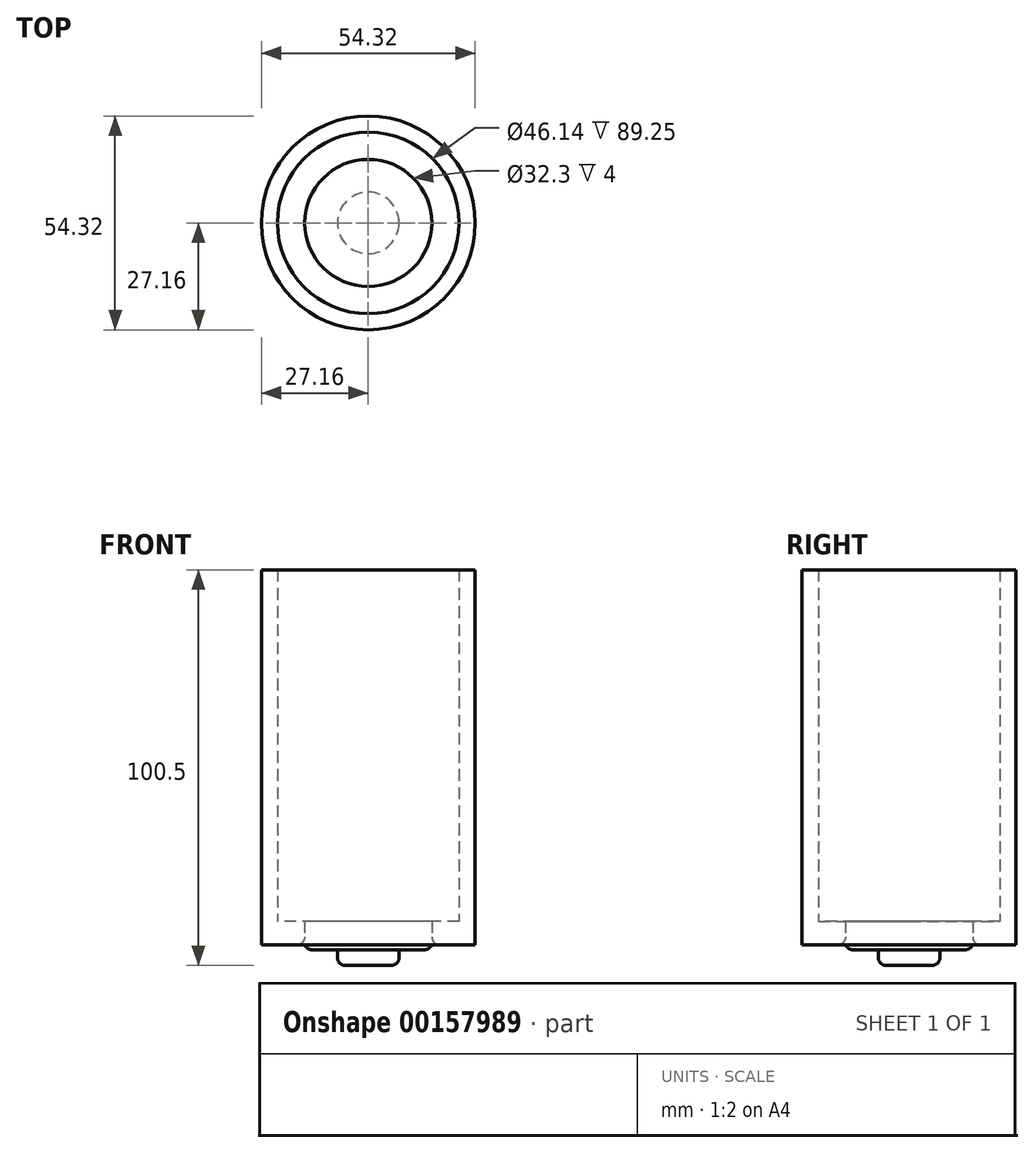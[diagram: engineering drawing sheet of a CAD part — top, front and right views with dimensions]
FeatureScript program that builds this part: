
annotation { "Feature Type Name" : "Feature", "Feature Type Description" : "" }
export const myFeature = defineFeature(function(context is Context, id is Id, definition is map)
    precondition{}
    {
        {
            var Q0;
            Q0=qCreatedBy(makeId("Top.planeOp"),FACE);
            var sketch = newSketch(context, id + "F0", { "sketchPlane" : qUnion([Q0])});
            skCircle(sketch, "E0", {"center": v(0, 0) * mm, "radius": 27.16 * mm});
            skCircle(sketch, "E1", {"center": v(0, 0) * mm, "radius": 7.81 * mm});
            skCircle(sketch, "E2", {"center": v(0, 0) * mm, "radius": 16.15 * mm});
            skCircle(sketch, "E3", {"center": v(0, 0) * mm, "radius": 23.07 * mm});
            skSolve(sketch);
        }
        {
            var Q0;
            Q0=makeQuery(id+"F0.imprint","IMPRINT",FACE,{"disambiguationData":[TD([[makeQuery(id+"F0.imprint","IMPRINT",EDGE,{"derivedFrom":sQuery(id+"F0.wireOp",EDGE,"E0")}),1.0]])]});
            extrude(context, id + "F1", {"entities" : qUnion([Q0]), "depth" : 95.25 * mm});
        }
        {
            var Q0;
            Q0=makeQuery(id+"F0.imprint","IMPRINT",FACE,{"disambiguationData":[TD([[makeQuery(id+"F0.imprint","IMPRINT",EDGE,{"derivedFrom":sQuery(id+"F0.wireOp",EDGE,"E2")}),-1.0]])]});
            extrude(context, id + "F2", {"entities" : qUnion([Q0]), "operationType" : NewBodyOperationType.ADD, "depth" : 6 * mm});
        }
        {
            var Q0;
            Q0=makeQuery(id+"F0.imprint","IMPRINT",FACE,{"disambiguationData":[TD([[makeQuery(id+"F0.imprint","IMPRINT",EDGE,{"derivedFrom":sQuery(id+"F0.wireOp",EDGE,"E1")}),-1.0]])]});
            extrude(context, id + "F3", {"entities" : qUnion([Q0]), "oppositeDirection" : true, "depth" : 1.25 * mm});
        }
        {
            var Q0;
            Q0=makeQuery(id+"F0.imprint","IMPRINT",FACE,{"disambiguationData":[TD([[makeQuery(id+"F0.imprint","IMPRINT",EDGE,{"derivedFrom":sQuery(id+"F0.wireOp",EDGE,"E1")}),1.0]])]});
            extrude(context, id + "F4", {"entities" : qUnion([Q0]), "operationType" : NewBodyOperationType.ADD, "oppositeDirection" : true, "depth" : 5.25 * mm});
        }
        {
            var Q0;
            Q0=makeQuery(id+"F4.opExtrude","CAP_EDGE",EDGE,{"disambiguationData":[OSD([sQuery(id+"F0.wireOp",EDGE,"E1")])],"isStart":false});
            var Q1;
            Q1=makeQuery(id+"F3.opExtrude","CAP_EDGE",EDGE,{"disambiguationData":[OSD([sQuery(id+"F0.wireOp",EDGE,"E2")])],"isStart":false});
            var Q2;
            Q2=makeQuery(id+"F2.opExtrude","CAP_EDGE",EDGE,{"disambiguationData":[OSD([sQuery(id+"F0.wireOp",EDGE,"E2")])],"isStart":true});
            fillet(context, id + "F5", {"entities" : qUnion([Q0, Q1, Q2]), "radius" : 2 * mm, "tangentPropagation" : true, "allowEdgeOverflow" : false});
        }
    });
